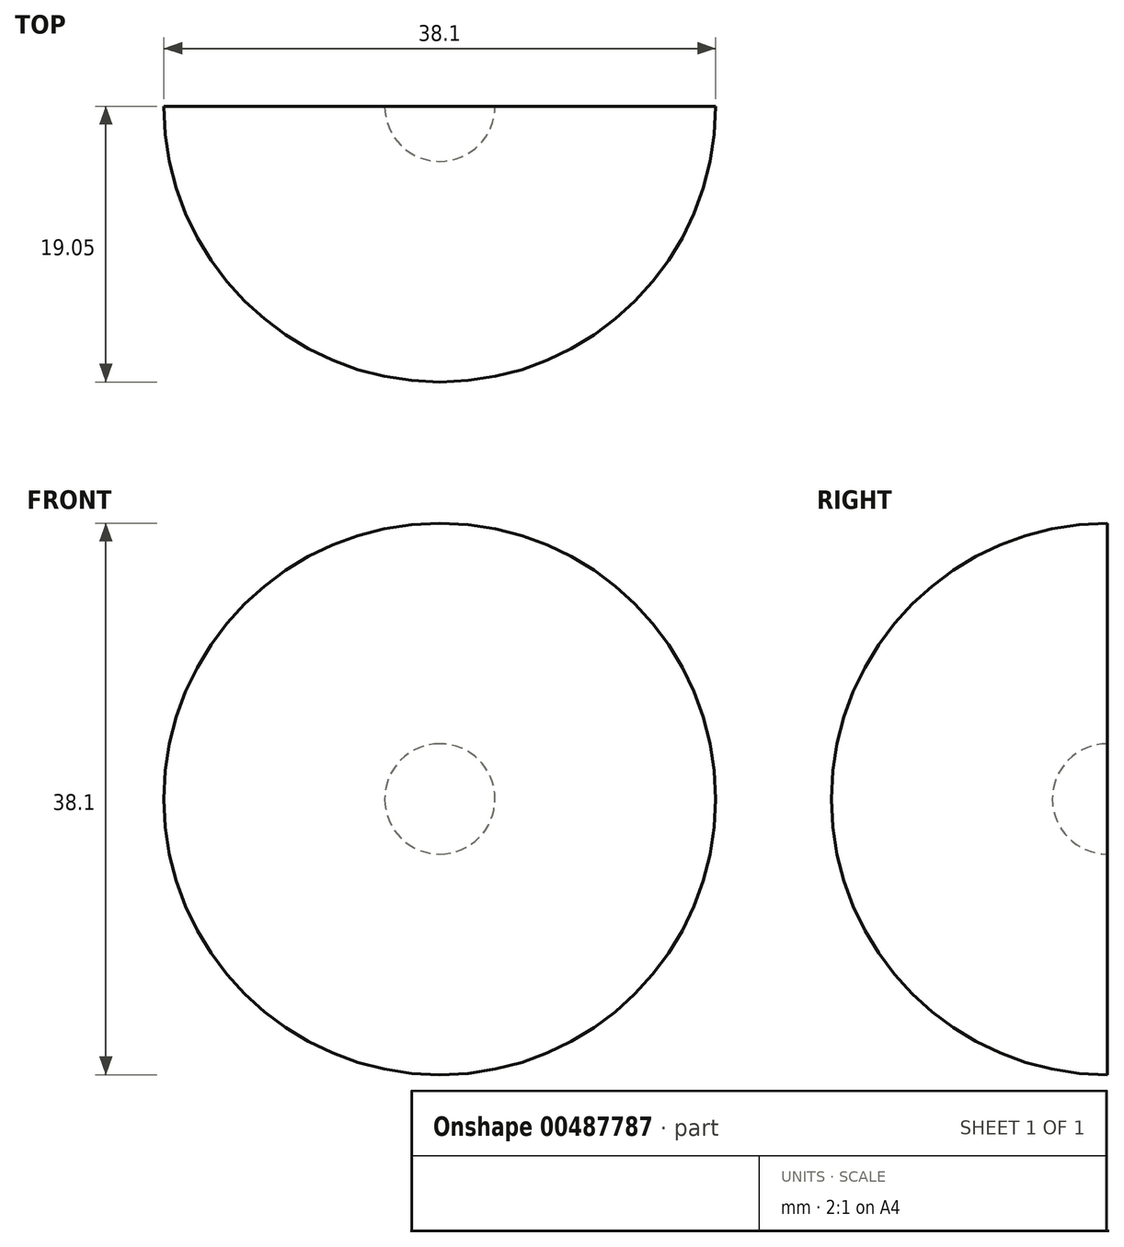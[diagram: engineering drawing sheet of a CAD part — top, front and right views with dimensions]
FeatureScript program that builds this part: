
annotation { "Feature Type Name" : "Feature", "Feature Type Description" : "" }
export const myFeature = defineFeature(function(context is Context, id is Id, definition is map)
    precondition{}
    {
        {
            var Q0;
            Q0=qCreatedBy(makeId("Front.planeOp"),FACE);
            var sketch = newSketch(context, id + "F0", { "sketchPlane" : qUnion([Q0])});
            skArc(sketch, "E0", {"start": v(0, -19.05) * mm, "mid": v(19.05, 0) * mm, "end": v(0, 19.05) * mm});
            skLineSegment(sketch, "E1", {"start": v(0, 19.05) * mm, "end": v(0, -19.05) * mm});
            skSolve(sketch);
        }
        {
            var Q0;
            Q0=makeQuery(id+"F0.imprint","IMPRINT",FACE,{"disambiguationData":[TD([[makeQuery(id+"F0.imprint","IMPRINT",EDGE,{"derivedFrom":sQuery(id+"F0.wireOp",EDGE,"E0")}),1.0]])]});
            var Q1;
            Q1=sQuery(id+"F0.wireOp",EDGE,"E1");
            revolve(context, id + "F1", {"entities" : qUnion([Q0]), "axis" : qUnion([Q1]), "revolveType" : RevolveType.ONE_DIRECTION, "angle" : 180 * degree});
        }
        {
            var Q0;
            Q0=makeQuery(id+"F1.opRevolve","CAP_FACE",FACE,{"disambiguationData":[OSD([sQuery(id+"F0.wireOp",EDGE,"E0"),sQuery(id+"F0.wireOp",EDGE,"E1")])],"isStart":true});
            shell(context, id + "F2", {"entities" : qUnion([Q0]), "thickness" : 15.24 * mm});
        }
    });
